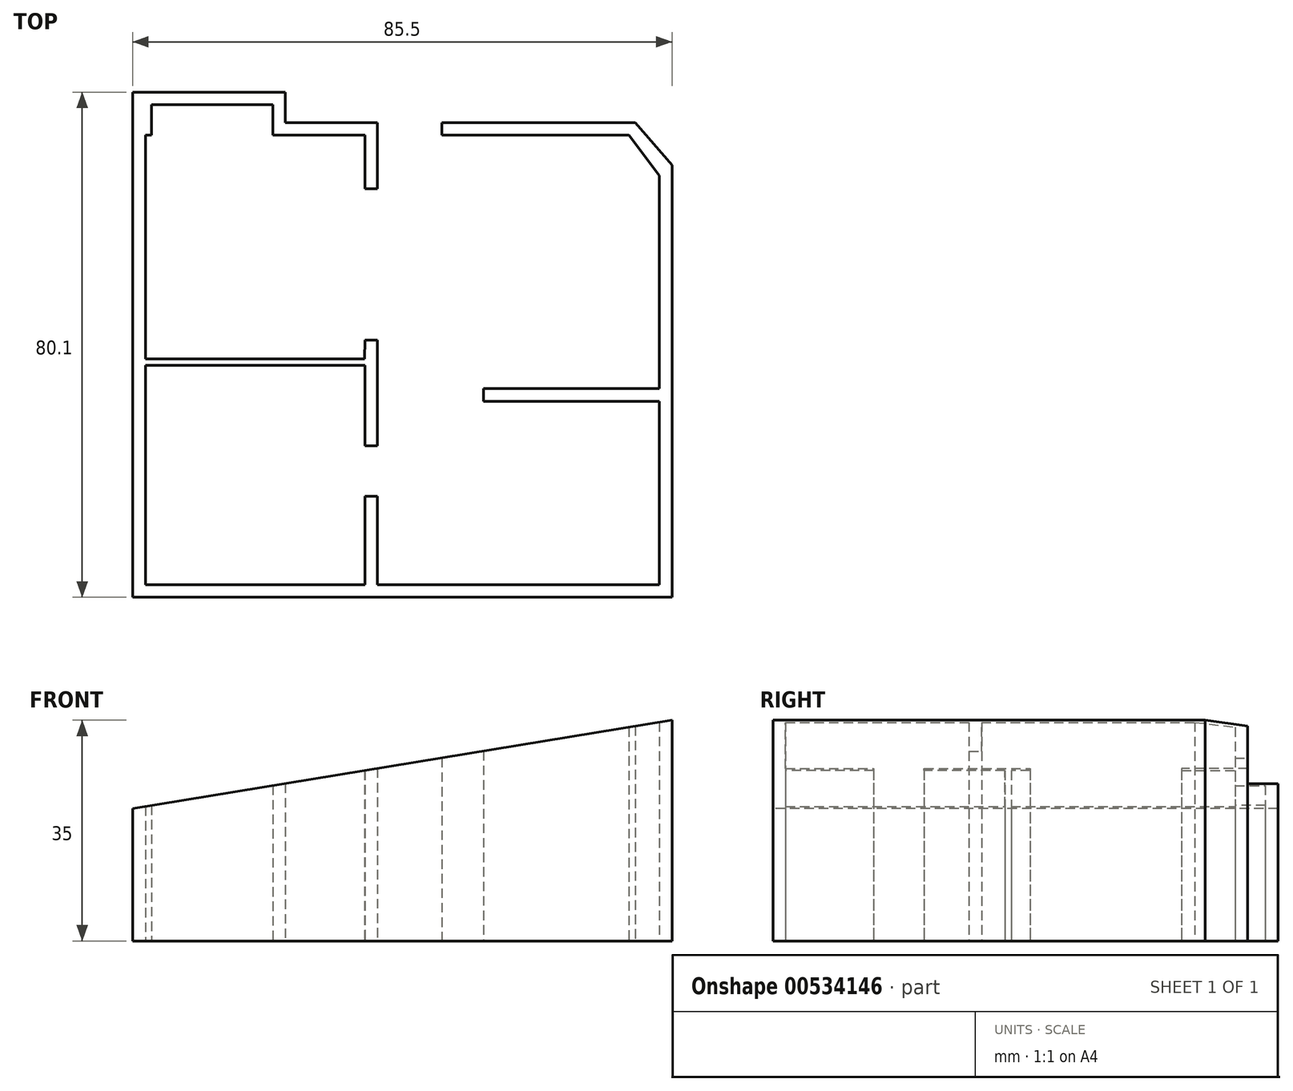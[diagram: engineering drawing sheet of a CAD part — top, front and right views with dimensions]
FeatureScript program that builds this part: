
annotation { "Feature Type Name" : "Feature", "Feature Type Description" : "" }
export const myFeature = defineFeature(function(context is Context, id is Id, definition is map)
    precondition{}
    {
        {
            var Q0;
            Q0=qCreatedBy(makeId("Top.planeOp"),FACE);
            var sketch = newSketch(context, id + "F0", { "sketchPlane" : qUnion([Q0])});
            skLineSegment(sketch, "E0", {"start": v(-50.26, 36.56) * mm, "end": v(-49.26, 36.56) * mm});
            skLineSegment(sketch, "E1", {"start": v(-49.26, 36.56) * mm, "end": v(-49.26, 41.36) * mm});
            skLineSegment(sketch, "E2", {"start": v(-49.26, 41.36) * mm, "end": v(-30.06, 41.36) * mm});
            skLineSegment(sketch, "E3", {"start": v(-30.06, 41.36) * mm, "end": v(-30.06, 36.56) * mm});
            skLineSegment(sketch, "E4", {"start": v(-30.06, 36.56) * mm, "end": v(-15.46, 36.56) * mm});
            skLineSegment(sketch, "E5", {"start": v(-15.46, 36.56) * mm, "end": v(-15.46, 28.06) * mm});
            skLineSegment(sketch, "E6", {"start": v(-15.46, 28.06) * mm, "end": v(-13.46, 28.06) * mm});
            skLineSegment(sketch, "E7", {"start": v(-13.46, 28.06) * mm, "end": v(-13.46, 38.56) * mm});
            skLineSegment(sketch, "E8", {"start": v(-28.06, 38.56) * mm, "end": v(-28.06, 43.36) * mm});
            skLineSegment(sketch, "E9", {"start": v(-28.06, 43.36) * mm, "end": v(-50.26, 43.36) * mm});
            skLineSegment(sketch, "E10", {"start": v(-46.13, 43.36) * mm, "end": v(-46.13, 41.36) * mm, "construction": true});
            skLineSegment(sketch, "E11", {"start": v(-30.06, 40.94) * mm, "end": v(-28.06, 40.94) * mm, "construction": true});
            skLineSegment(sketch, "E12", {"start": v(-15.46, 32.31) * mm, "end": v(-13.46, 32.31) * mm, "construction": true});
            skLineSegment(sketch, "E13", {"start": v(-13.46, 28.06) * mm, "end": v(-13.46, 4.06) * mm, "construction": true});
            skLineSegment(sketch, "E14", {"start": v(-15.46, 4.06) * mm, "end": v(-13.46, 4.06) * mm});
            skLineSegment(sketch, "E15", {"start": v(-13.46, 4.06) * mm, "end": v(-13.46, -12.74) * mm});
            skLineSegment(sketch, "E16", {"start": v(-13.46, -12.74) * mm, "end": v(-15.46, -12.74) * mm});
            skLineSegment(sketch, "E17", {"start": v(-15.46, -12.74) * mm, "end": v(-15.46, 0.06) * mm});
            skLineSegment(sketch, "E18", {"start": v(-15.46, 0.06) * mm, "end": v(-50.26, 0.06) * mm});
            skLineSegment(sketch, "E19", {"start": v(-50.26, 0.06) * mm, "end": v(-50.26, -34.74) * mm});
            skLineSegment(sketch, "E20", {"start": v(-50.26, -34.74) * mm, "end": v(-15.46, -34.74) * mm});
            skLineSegment(sketch, "E21", {"start": v(-15.46, -34.74) * mm, "end": v(-15.46, -20.74) * mm});
            skLineSegment(sketch, "E22", {"start": v(-15.46, -20.74) * mm, "end": v(-13.46, -20.74) * mm});
            skLineSegment(sketch, "E23", {"start": v(-13.46, -20.74) * mm, "end": v(-13.46, -34.74) * mm});
            skLineSegment(sketch, "E24", {"start": v(-13.46, -36.74) * mm, "end": v(-52.26, -36.74) * mm});
            skLineSegment(sketch, "E25", {"start": v(-52.26, -36.74) * mm, "end": v(-52.26, 43.36) * mm});
            skLineSegment(sketch, "E26", {"start": v(-13.46, -12.74) * mm, "end": v(-13.46, -20.74) * mm, "construction": true});
            skLineSegment(sketch, "E27", {"start": v(-28.06, 38.56) * mm, "end": v(-13.46, 38.56) * mm});
            skLineSegment(sketch, "E28", {"start": v(-52.26, -18.27) * mm, "end": v(-50.26, -18.27) * mm, "construction": true});
            skLineSegment(sketch, "E29", {"start": v(-50.26, 43.36) * mm, "end": v(-52.26, 43.36) * mm});
            skLineSegment(sketch, "E30", {"start": v(-50.26, 36.56) * mm, "end": v(-50.26, 1.06) * mm});
            skLineSegment(sketch, "E31", {"start": v(-50.26, 1.06) * mm, "end": v(-15.49, 1.06) * mm});
            skLineSegment(sketch, "E32", {"start": v(-15.49, 1.06) * mm, "end": v(-15.46, 4.06) * mm});
            skLineSegment(sketch, "E33", {"start": v(-39.44, 1.06) * mm, "end": v(-39.44, 0.06) * mm, "construction": true});
            skLineSegment(sketch, "E34", {"start": v(-23.83, 36.56) * mm, "end": v(-23.83, 1.06) * mm, "construction": true});
            skLineSegment(sketch, "E35", {"start": v(-13.46, 38.56) * mm, "end": v(-3.26, 38.56) * mm, "construction": true});
            skLineSegment(sketch, "E36", {"start": v(-3.26, 38.56) * mm, "end": v(-3.26, 36.56) * mm});
            skLineSegment(sketch, "E37", {"start": v(-3.26, 36.56) * mm, "end": v(26.44, 36.56) * mm});
            skLineSegment(sketch, "E38", {"start": v(26.44, 36.56) * mm, "end": v(31.24, 30.14) * mm});
            skLineSegment(sketch, "E39", {"start": v(31.24, 30.14) * mm, "end": v(31.24, -3.64) * mm});
            skLineSegment(sketch, "E40", {"start": v(31.24, -3.64) * mm, "end": v(3.34, -3.64) * mm});
            skLineSegment(sketch, "E41", {"start": v(3.34, -3.64) * mm, "end": v(3.34, -5.64) * mm});
            skLineSegment(sketch, "E42", {"start": v(3.34, -5.64) * mm, "end": v(31.24, -5.64) * mm});
            skLineSegment(sketch, "E43", {"start": v(31.24, -5.64) * mm, "end": v(31.24, -34.74) * mm});
            skLineSegment(sketch, "E44", {"start": v(31.24, -34.74) * mm, "end": v(-13.46, -34.74) * mm});
            skLineSegment(sketch, "E45", {"start": v(33.24, -36.74) * mm, "end": v(33.24, 31.82) * mm});
            skLineSegment(sketch, "E46", {"start": v(33.24, 31.82) * mm, "end": v(27.44, 38.56) * mm});
            skLineSegment(sketch, "E47", {"start": v(27.44, 38.56) * mm, "end": v(-3.26, 38.56) * mm});
            skLineSegment(sketch, "E48", {"start": v(-13.46, -36.74) * mm, "end": v(33.24, -36.74) * mm});
            skLineSegment(sketch, "E49", {"start": v(10.05, 36.56) * mm, "end": v(10.05, -3.64) * mm, "construction": true});
            skLineSegment(sketch, "E50", {"start": v(31.24, 14.22) * mm, "end": v(-13.46, 14.22) * mm, "construction": true});
            skPoint(sketch, "E50.endSnap0", {"position": v(-13.46, 16.06) * mm});
            skLineSegment(sketch, "E51", {"start": v(10.05, -5.64) * mm, "end": v(10.05, -34.74) * mm, "construction": true});
            skLineSegment(sketch, "E52", {"start": v(40.88, -34.74) * mm, "end": v(40.88, -36.74) * mm, "construction": true});
            skLineSegment(sketch, "E53", {"start": v(31.24, 8.04) * mm, "end": v(33.24, 8.04) * mm, "construction": true});
            skSolve(sketch);
        }
        {
            var Q0;
            Q0 = qSketchRegion(id + "F0", true);
            extrude(context, id + "F1", {"entities" : qUnion([Q0]), "depth" : 35 * mm, "offsetDistance" : 25 * mm});
        }
        {
            var Q0;
            Q0=makeQuery(id+"F1.opExtrude","SWEPT_FACE",FACE,{"disambiguationData":[OSD([sQuery(id+"F0.wireOp",EDGE,"E24"),sQuery(id+"F0.wireOp",EDGE,"E48")])]});
            var sketch = newSketch(context, id + "F2", { "sketchPlane" : qUnion([Q0])});
            skLineSegment(sketch, "E54", {"start": v(-52.26, 21) * mm, "end": v(33.24, 35) * mm});
            skLineSegment(sketch, "E55", {"start": v(33.24, 35) * mm, "end": v(27.84, 67.96) * mm});
            skLineSegment(sketch, "E56", {"start": v(27.84, 67.96) * mm, "end": v(-52.26, 61.38) * mm});
            skLineSegment(sketch, "E57", {"start": v(-52.26, 61.38) * mm, "end": v(-52.26, 21) * mm});
            skLineSegment(sketch, "E58", {"start": v(-52.26, 21) * mm, "end": v(-52.26, 0) * mm, "construction": true});
            skSolve(sketch);
        }
        {
            var Q0;
            Q0 = qSketchRegion(id + "F2", true);
            extrude(context, id + "F3", {"entities" : qUnion([Q0]), "operationType" : NewBodyOperationType.REMOVE, "oppositeDirection" : true, "depth" : 90 * mm, "offsetDistance" : 25 * mm});
        }
    });
